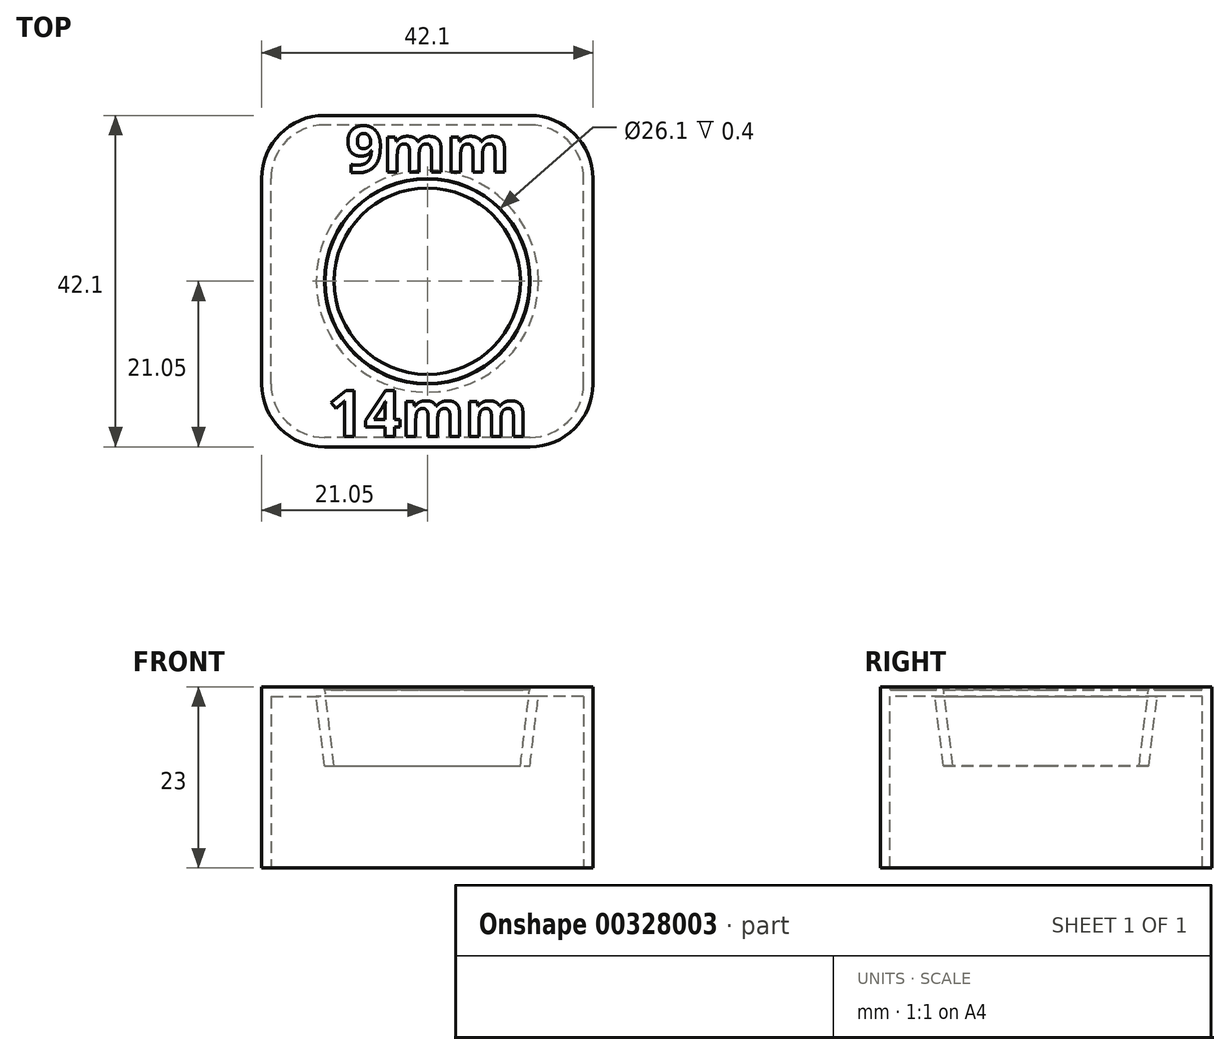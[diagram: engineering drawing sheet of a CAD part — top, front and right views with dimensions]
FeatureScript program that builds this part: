
annotation { "Feature Type Name" : "Feature", "Feature Type Description" : "" }
export const myFeature = defineFeature(function(context is Context, id is Id, definition is map)
    precondition{}
    {
        {
            var Q0;
            Q0=qCreatedBy(makeId("Top.planeOp"),FACE);
            var sketch = newSketch(context, id + "F0", { "sketchPlane" : qUnion([Q0])});
            skCircle(sketch, "E0", {"center": v(0, 0) * mm, "radius": 13.05 * mm});
            skLineSegment(sketch, "E1.bottom", {"start": v(21.05, -21.05) * mm, "end": v(-21.05, -21.05) * mm});
            skLineSegment(sketch, "E1.top", {"start": v(21.05, 21.05) * mm, "end": v(-21.05, 21.05) * mm});
            skLineSegment(sketch, "E1.left", {"start": v(21.05, -21.05) * mm, "end": v(21.05, 21.05) * mm});
            skLineSegment(sketch, "E1.right", {"start": v(-21.05, -21.05) * mm, "end": v(-21.05, 21.05) * mm});
            skSolve(sketch);
        }
        {
            var Q0;
            Q0=makeQuery(id+"F0.imprint","IMPRINT",FACE,{"disambiguationData":[TD([[makeQuery(id+"F0.imprint","IMPRINT",EDGE,{"derivedFrom":sQuery(id+"F0.wireOp",EDGE,"E0")}),-1.0]])]});
            var Q1;
            Q1=makeQuery(id+"F0.imprint","IMPRINT",FACE,{"disambiguationData":[TD([[makeQuery(id+"F0.imprint","IMPRINT",EDGE,{"derivedFrom":sQuery(id+"F0.wireOp",EDGE,"E0")}),1.0]])]});
            extrude(context, id + "F1", {"entities" : qUnion([Q0, Q1]), "oppositeDirection" : true, "depth" : 23 * mm});
        }
        {
            var Q0;
            Q0=makeQuery(id+"F1.opExtrude","CAP_FACE",FACE,{"disambiguationData":[OSD([sQuery(id+"F0.wireOp",EDGE,"E1.bottom"),sQuery(id+"F0.wireOp",EDGE,"E1.top"),sQuery(id+"F0.wireOp",EDGE,"E1.left"),sQuery(id+"F0.wireOp",EDGE,"E1.right")])],"isStart":false});
            var sketch = newSketch(context, id + "F2", { "sketchPlane" : qUnion([Q0])});
            skCircle(sketch, "E2.11", {"center": v(0, 0) * mm, "radius": 13.05 * mm, "construction": true});
            skCircle(sketch, "E2.18", {"center": v(0, 0) * mm, "radius": 13.05 * mm, "construction": true});
            skCircle(sketch, "E3", {"center": v(0, 0) * mm, "radius": 10.25 * mm});
            skSolve(sketch);
        }
        {
            var Q0;
            Q0=makeQuery(id+"F0.imprint","IMPRINT",FACE,{"disambiguationData":[TD([[makeQuery(id+"F0.imprint","IMPRINT",EDGE,{"derivedFrom":sQuery(id+"F0.wireOp",EDGE,"E0")}),1.0]])]});
            var Q1;
            Q1=makeQuery(id+"F2.imprint","IMPRINT",FACE,{"disambiguationData":[TD([[makeQuery(id+"F2.imprint","IMPRINT",EDGE,{"derivedFrom":sQuery(id+"F2.wireOp",EDGE,"E3")}),1.0]])]});
            loft(context, id + "F3", {"sheetProfilesArray" : [{ "sheetProfileEntities" : qUnion([Q0]) }, { "sheetProfileEntities" : qUnion([Q1]) }]});
        }
        {
            var Q0;
            Q0=makeQuery(id+"F3.opLoft","SWEPT_BODY",BODY,{"disambiguationData":[OSD([makeQuery(id+"F0.imprint","IMPRINT",FACE,{"disambiguationData":[TD([[makeQuery(id+"F0.imprint","IMPRINT",EDGE,{"derivedFrom":sQuery(id+"F0.wireOp",EDGE,"E0")}),1.0]])]}),makeQuery(id+"F2.imprint","IMPRINT",FACE,{"disambiguationData":[TD([[makeQuery(id+"F2.imprint","IMPRINT",EDGE,{"derivedFrom":sQuery(id+"F2.wireOp",EDGE,"E3")}),1.0]])]})])]});
            var Q1;
            Q1=makeQuery(id+"F1.opExtrude","SWEPT_BODY",BODY,{"disambiguationData":[OSD([sQuery(id+"F0.wireOp",EDGE,"E1.bottom"),sQuery(id+"F0.wireOp",EDGE,"E1.top"),sQuery(id+"F0.wireOp",EDGE,"E1.left"),sQuery(id+"F0.wireOp",EDGE,"E1.right")])]});
            booleanBodies(context, id + "F4", {"operationType" : BooleanOperationType.SUBTRACTION, "tools" : qUnion([Q0]), "targets" : qUnion([Q1])});
        }
        {
            var Q0;
            Q0=makeQuery(id+"F1.opExtrude","SWEPT_EDGE",EDGE,{"disambiguationData":[OSD([sQuery(id+"F0.wireOp",EDGE,"E1.bottom"),sQuery(id+"F0.wireOp",EDGE,"E1.right")])]});
            var Q1;
            Q1=makeQuery(id+"F1.opExtrude","SWEPT_EDGE",EDGE,{"disambiguationData":[OSD([sQuery(id+"F0.wireOp",EDGE,"E1.top"),sQuery(id+"F0.wireOp",EDGE,"E1.right")])]});
            var Q2;
            Q2=makeQuery(id+"F1.opExtrude","SWEPT_EDGE",EDGE,{"disambiguationData":[OSD([sQuery(id+"F0.wireOp",EDGE,"E1.top"),sQuery(id+"F0.wireOp",EDGE,"E1.left")])]});
            var Q3;
            Q3=makeQuery(id+"F1.opExtrude","SWEPT_EDGE",EDGE,{"disambiguationData":[OSD([sQuery(id+"F0.wireOp",EDGE,"E1.bottom"),sQuery(id+"F0.wireOp",EDGE,"E1.left")])]});
            fillet(context, id + "F5", {"entities" : qUnion([Q0, Q1, Q2, Q3]), "radius" : 8 * mm, "tangentPropagation" : true, "allowEdgeOverflow" : false});
        }
        {
            var Q0;
            Q0=makeQuery(id+"F1.opExtrude","CAP_FACE",FACE,{"disambiguationData":[OSD([sQuery(id+"F0.wireOp",EDGE,"E1.bottom"),sQuery(id+"F0.wireOp",EDGE,"E1.top"),sQuery(id+"F0.wireOp",EDGE,"E1.left"),sQuery(id+"F0.wireOp",EDGE,"E1.right")])],"isStart":false});
            shell(context, id + "F6", {"entities" : qUnion([Q0]), "thickness" : 1.2 * mm});
        }
        {
            var Q0;
            Q0=makeQuery(id+"F1.opExtrude","CAP_FACE",FACE,{"disambiguationData":[OSD([sQuery(id+"F0.wireOp",EDGE,"E1.bottom"),sQuery(id+"F0.wireOp",EDGE,"E1.top"),sQuery(id+"F0.wireOp",EDGE,"E1.left"),sQuery(id+"F0.wireOp",EDGE,"E1.right")])],"isStart":true});
            var sketch = newSketch(context, id + "F7", { "sketchPlane" : qUnion([Q0])});
            skText(sketch, "E4", { "text": "14mm", "fontName": "OpenSans-Bold.ttf"});
            skText(sketch, "E5", { "text": "9mm", "fontName": "OpenSans-Bold.ttf"});
            skCircle(sketch, "E6.0", {"center": v(0, 0) * mm, "radius": 13.05 * mm});
            const initialGuessF7  = {"E4": [-0.01268, -0.01975, 1, 0, 0.0059], "E5": [-0.01035, 0.01385, 1, 0, 0.0059]};
            skSetInitialGuess(sketch, initialGuessF7);
            skSolve(sketch);
        }
        {
            var Q0;
            Q0=qSketchRegion(id+"F7",true);
            extrude(context, id + "F8", {"entities" : qUnion([Q0]), "operationType" : NewBodyOperationType.REMOVE, "oppositeDirection" : true, "depth" : .4 * mm});
        }
        {
            var Q0;
            {var subQ0=sQuery(id+"F0.wireOp",EDGE,"E1.right");var subQ1=sQuery(id+"F0.wireOp",EDGE,"E1.left");var subQ2=sQuery(id+"F0.wireOp",EDGE,"E1.top");var subQ3=sQuery(id+"F0.wireOp",EDGE,"E1.bottom");Q0=makeQuery(id+"F6.opShell","OFFSET_FACE",FACE,{"disambiguationData":[OSD([subQ3,subQ2,subQ1,subQ0]),TDD([makeQuery(id+"F1.opExtrude","CAP_FACE",FACE,{"disambiguationData":[OSD([subQ3,subQ2,subQ1,subQ0])],"isStart":false})])]});}
            var sketch = newSketch(context, id + "F9", { "sketchPlane" : qUnion([Q0])});
            skLineSegment(sketch, "E7.bottom", {"start": v(14.08, -14.6) * mm, "end": v(-14.08, -14.6) * mm});
            skLineSegment(sketch, "E7.top", {"start": v(14.08, 14.6) * mm, "end": v(-14.08, 14.6) * mm});
            skLineSegment(sketch, "E7.left", {"start": v(14.08, -14.6) * mm, "end": v(14.08, 14.6) * mm});
            skLineSegment(sketch, "E7.right", {"start": v(-14.08, -14.6) * mm, "end": v(-14.08, 14.6) * mm});
            skPoint(sketch, "E7.middle", {"position": v(0, 0) * mm});
            skSolve(sketch);
        }
        {
            var Q0;
            Q0 = qSketchRegion(id + "F9", true);
            extrude(context, id + "F10", {"entities" : qUnion([Q0]), "operationType" : NewBodyOperationType.REMOVE, "oppositeDirection" : true, "depth" : 13 * mm});
        }
    });
